# Revit family: Hager-FW-IP30-With_Door-With_notch-syst-NoHosted-AT-de
name_source: partatom
category: Electrical Equipment
units: mm (PartAtom-declared; Revit-internal decimal feet)

## family parameters
Always vertical = Yes
Cut with Voids When Loaded = No
Panel Configuration = Two Columns, Circuits Across
Part Type = Panelboard
Room Calculation Point = No
Round Connector Dimension = Use Diameter
Shared = No
Work Plane-Based = Yes

## types (15) — shared parameters
Default Elevation = 1219 mm
EF000003 - Montageart = EV000128 - Hohlwand
EF000007 - Farbe = EV000202 - weiß
EF000049 - Tiefe = 125 mm  [stored 0.410105 ft]
EF000118 - Mit Montageplatte = No
EF000218 - Einbautiefe = 112 mm  [stored 0.367454 ft]
EF000339 - Art der Abdeckung = EV004216 - Tür
EF001062 - EMV-Ausführung = No
EF001088 - Anbaumöglichkeit = Yes
EF001131 - Innentiefe = 112 mm  [stored 0.367454 ft]
EF001596 - Werkstoff des Gehäuses = EV000179 - Stahl
EF002950 - Breite in Teilungseinheiten = 12
EF004462 - Art der Schließung = EV000154 - sonstige
EF005474 - Schutzart (IP) = EV006410 - IP30
EF006244 - Transparenter Deckel/Tür = No
EF006306 - Mit Schloss = No
EF009212 - Ausführung Deckel = EV009916 - mit Ausschnitt
EF015776 - Erdungsklemmenblock = Yes
EF015941 - Signaldurchlassende Tür = No
HG000002 - Mit tür = Yes
HG000003 - Bereich = FW
HG000005 - Dicke = 3 mm  [stored 0.00984252 ft]
HG000006 - Unterputz = Yes
HG000011 - Leere Reihen von unten = No
HG000017 - Distanz zwischen den Polen = 18 mm  [stored 0.0590551 ft]
Manufacturer = Hager
Type Comments = FW
zero-valued in all types: HG000007 - Anzahl der leeren Spalten, HG000008 - Anzahl der leeren Reihen

## per-type parameters (varying)
| type | EF000008 - Breite | EF000040 - Höhe | EF000116 - RAL-Nummer | EF000266 - Anzahl der Reihen | EF000332 - Einbauhöhe | EF000846 - Einbaubreite | EF001134 - DIN-Schiene | EF015777 - Neutralleiterklemmenblock | HG000001 - Anzahl der Spalten | HG000004 - Herstellerreferenz | HG000009 - Doppelflügeligen Tür | HG000010 - Asymmetrische Türen | Model |
| Unterputz IP30 B353 H1003 T125 12 Teilungseinheiten - FWU61S | 353 mm  [stored 1.15814 ft] | 1003 mm  [stored 3.29068 ft] | 9010 | 6 | 952 mm  [stored 3.12336 ft] | 310 mm  [stored 1.01706 ft] | Yes | No | 1 | FWU61S | No | No | FWU61S |
| Unterputz IP30 B353 H1153 T125 12 Teilungseinheiten - FWU71S | 353 mm  [stored 1.15814 ft] | 1153 mm | 9010 | 7 | 1102 mm  [stored 3.61549 ft] | 310 mm  [stored 1.01706 ft] | Yes | No | 1 | FWU71S | No | No | FWU71S |
| Unterputz IP30 B353 H553 T125 12 Teilungseinheiten - FWU31S | 353 mm  [stored 1.15814 ft] | 553 mm  [stored 1.8143 ft] | 9010 | 3 | 502 mm  [stored 1.64698 ft] | 310 mm  [stored 1.01706 ft] | Yes | Yes | 1 | FWU31S | No | No | FWU31S |
| Unterputz IP30 B353 H703 T125 12 Teilungseinheiten - FWU41S | 353 mm  [stored 1.15814 ft] | 703 mm  [stored 2.30643 ft] | 9010 | 4 | 652 mm  [stored 2.13911 ft] | 310 mm  [stored 1.01706 ft] | Yes | No | 1 | FWU41S | No | No | FWU41S |
| Unterputz IP30 B353 H853 T125 12 Teilungseinheiten - FWU51S | 353 mm  [stored 1.15814 ft] | 853 mm  [stored 2.79856 ft] | 9010 | 5 | 802 mm  [stored 2.63123 ft] | 310 mm  [stored 1.01706 ft] | Yes | No | 1 | FWU51S | No | No | FWU51S |
| Unterputz IP30 B603 H1003 T125 12 Teilungseinheiten - FWU62S | 603 mm | 1003 mm  [stored 3.29068 ft] | 9010 | 12 | 952 mm  [stored 3.12336 ft] | 560 mm  [stored 1.83727 ft] | Yes | No | 2 | FWU62S | No | No | FWU62S |
| Unterputz IP30 B603 H1153 T125 12 Teilungseinheiten - FWU72S | 603 mm | 1153 mm | 9010 | 14 | 1102 mm  [stored 3.61549 ft] | 560 mm  [stored 1.83727 ft] | Yes | No | 2 | FWU72S | No | No | FWU72S |
| Unterputz IP30 B603 H553 T125 12 Teilungseinheiten - FWU32S | 603 mm | 553 mm  [stored 1.8143 ft] | 9010 | 6 | 502 mm  [stored 1.64698 ft] | 560 mm  [stored 1.83727 ft] | Yes | No | 2 | FWU32S | No | No | FWU32S |
| Unterputz IP30 B603 H703 T125 12 Teilungseinheiten - FWU42S | 603 mm | 703 mm  [stored 2.30643 ft] | 9010 | 8 | 652 mm  [stored 2.13911 ft] | 560 mm  [stored 1.83727 ft] | Yes | No | 2 | FWU42S | No | No | FWU42S |
| Unterputz IP30 B603 H853 T125 12 Teilungseinheiten - FWU52S | 603 mm | 853 mm  [stored 2.79856 ft] | 9010 | 10 | 802 mm  [stored 2.63123 ft] | 560 mm  [stored 1.83727 ft] | Yes | No | 2 | FWU52S | No | No | FWU52S |
| Unterputz IP30 B853 H1003 T125 12 Teilungseinheiten - FWU63S | 853 mm  [stored 2.79856 ft] | 1003 mm  [stored 3.29068 ft] | 9010 | 18 | 952 mm  [stored 3.12336 ft] | 810 mm | Yes | No | 3 | FWU63S | Yes | Yes | FWU63S |
| Unterputz IP30 B853 H1153 T125 12 Teilungseinheiten - FWU73S | 853 mm  [stored 2.79856 ft] | 1153 mm | 9010 | 21 | 1102 mm  [stored 3.61549 ft] | 810 mm | Yes | Yes | 3 | FWU73S | Yes | Yes | FWU73S |
| Unterputz IP30 B853 H553 T125 12 Teilungseinheiten - FWU33S | 853 mm  [stored 2.79856 ft] | 553 mm  [stored 1.8143 ft] | 9010 | 9 | 502 mm  [stored 1.64698 ft] | 810 mm | Yes | No | 3 | FWU33S | Yes | Yes | FWU33S |
| Unterputz IP30 B853 H703 T125 12 Teilungseinheiten - FWU43S | 853 mm  [stored 2.79856 ft] | 703 mm  [stored 2.30643 ft] | 9010 | 12 | 652 mm  [stored 2.13911 ft] | 810 mm | Yes | No | 3 | FWU43S | Yes | Yes | FWU43S |
| Unterputz IP30 B853 H853 T125 12 Teilungseinheiten - FWU53S | 853 mm  [stored 2.79856 ft] | 853 mm  [stored 2.79856 ft] |  | 15 | 802 mm  [stored 2.63123 ft] | 810 mm | No | No | 3 | FWU53S | Yes | Yes | FWU53S |

note: [stored X ft] marks values corroborated as IEEE doubles in the binary element streams (Revit-internal decimal feet)

## geometry (parser evidence)
native form markers: Sweep x13
no freeform markers — native parametric forms only
